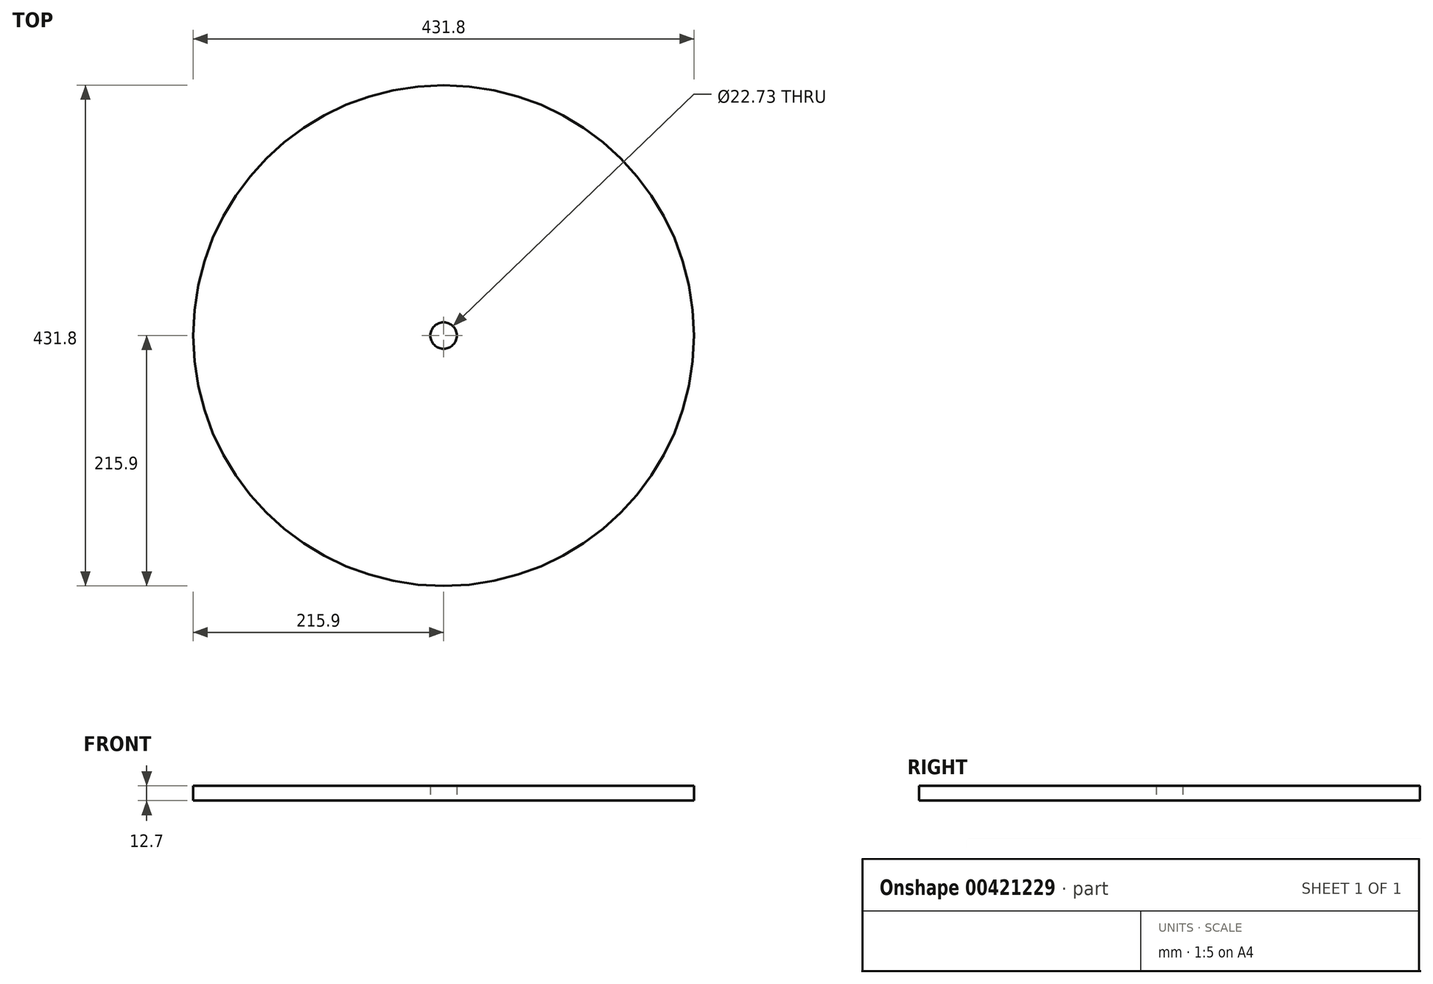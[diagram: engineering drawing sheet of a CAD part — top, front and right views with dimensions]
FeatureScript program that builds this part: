
annotation { "Feature Type Name" : "Feature", "Feature Type Description" : "" }
export const myFeature = defineFeature(function(context is Context, id is Id, definition is map)
    precondition{}
    {
        {
            var Q0;
            Q0=qCreatedBy(makeId("Top.planeOp"),FACE);
            var sketch = newSketch(context, id + "F0", { "sketchPlane" : qUnion([Q0])});
            skCircle(sketch, "E0", {"center": v(0, 0) * mm, "radius": 215.9 * mm});
            skCircle(sketch, "E1", {"center": v(0, 0) * mm, "radius": 11.37 * mm});
            skSolve(sketch);
        }
        {
            var Q0;
            Q0=makeQuery(id+"F0.imprint","IMPRINT",FACE,{"disambiguationData":[TD([[makeQuery(id+"F0.imprint","IMPRINT",EDGE,{"derivedFrom":sQuery(id+"F0.wireOp",EDGE,"E0")}),1.0]])]});
            extrude(context, id + "F1", {"entities" : qUnion([Q0]), "depth" : 12.7 * mm});
        }
    });
